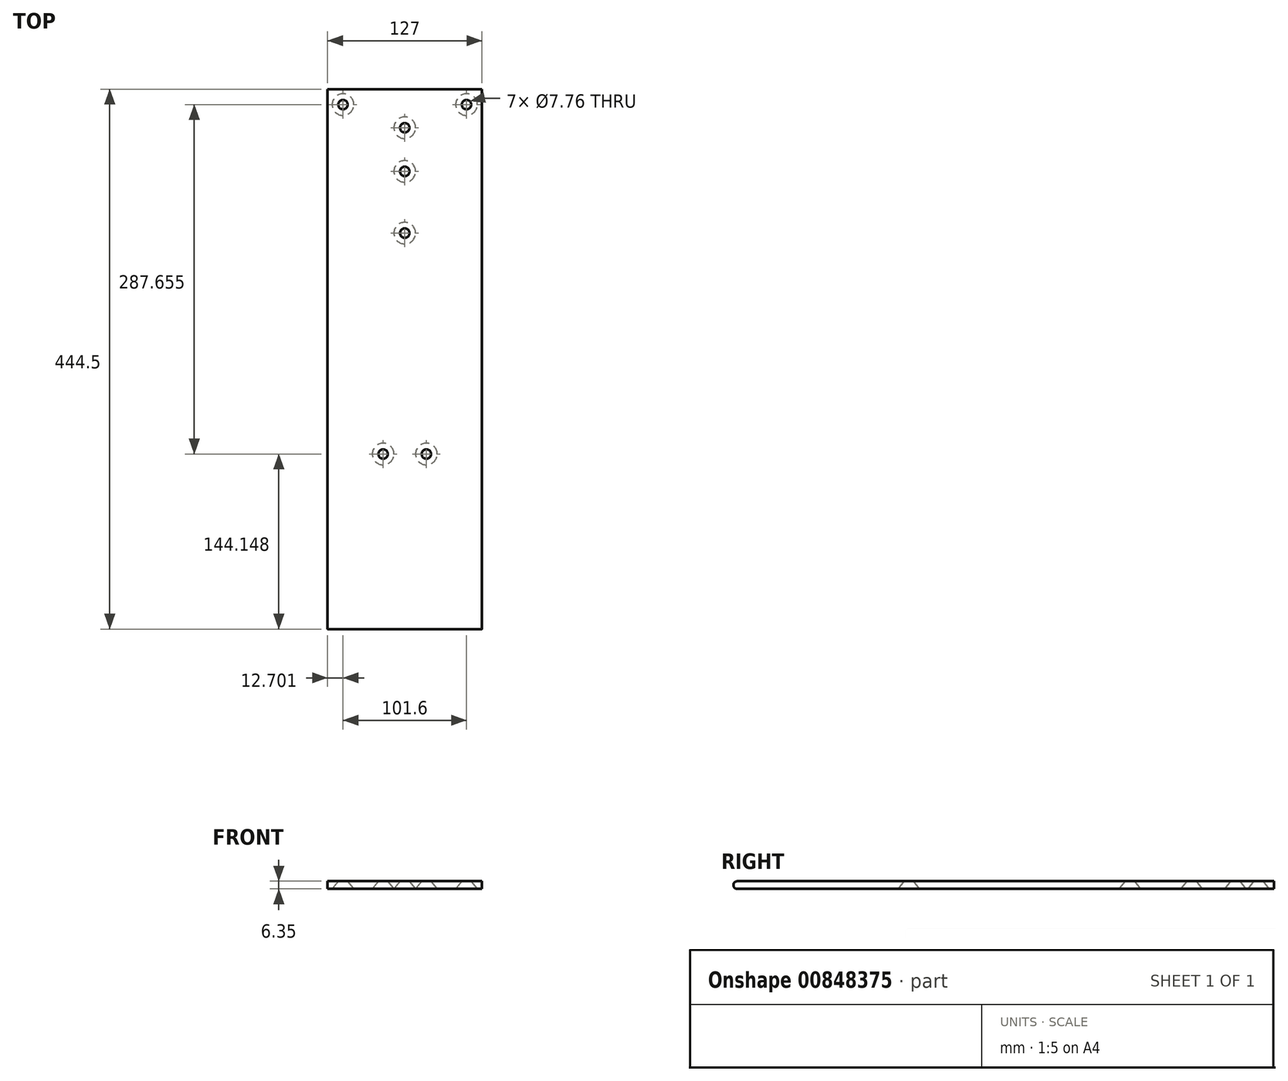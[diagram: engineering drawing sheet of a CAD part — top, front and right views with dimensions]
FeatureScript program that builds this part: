
annotation { "Feature Type Name" : "Feature", "Feature Type Description" : "" }
export const myFeature = defineFeature(function(context is Context, id is Id, definition is map)
    precondition{}
    {
        {
            var Q0;
            Q0=qCreatedBy(makeId("Top.planeOp"),FACE);
            var sketch = newSketch(context, id + "F0", { "sketchPlane" : qUnion([Q0])});
            skLineSegment(sketch, "E0.bottom", {"start": v(-72.87, 261.97) * mm, "end": v(54.13, 261.97) * mm});
            skLineSegment(sketch, "E0.top", {"start": v(-72.87, -182.53) * mm, "end": v(54.13, -182.53) * mm});
            skLineSegment(sketch, "E0.left", {"start": v(-72.87, 261.97) * mm, "end": v(-72.87, -182.53) * mm});
            skLineSegment(sketch, "E0.right", {"start": v(54.13, 261.97) * mm, "end": v(54.13, -182.53) * mm});
            skSolve(sketch);
        }
        {
            var Q0;
            Q0=makeQuery(id+"F0.imprint","IMPRINT",FACE,{"disambiguationData":[TD([[makeQuery(id+"F0.imprint","IMPRINT",EDGE,{"derivedFrom":sQuery(id+"F0.wireOp",EDGE,"E0.bottom")}),-1.0]])]});
            extrude(context, id + "F1", {"entities" : qUnion([Q0]), "depth" : 6.35 * mm, "offsetDistance" : 25.4 * mm});
        }
        {
            var Q0;
            Q0=makeQuery(id+"F1.opExtrude","CAP_FACE",FACE,{"disambiguationData":[OSD([sQuery(id+"F0.wireOp",EDGE,"E0.bottom"),sQuery(id+"F0.wireOp",EDGE,"E0.top"),sQuery(id+"F0.wireOp",EDGE,"E0.left"),sQuery(id+"F0.wireOp",EDGE,"E0.right")])],"isStart":false});
            var sketch = newSketch(context, id + "F2", { "sketchPlane" : qUnion([Q0])});
            skLineSegment(sketch, "E1", {"start": v(35.72, 199.74) * mm, "end": v(19.2, 185.77) * mm});
            skLineSegment(sketch, "E2", {"start": v(-54.45, 199.74) * mm, "end": v(-37.94, 185.77) * mm});
            skLineSegment(sketch, "E3", {"start": v(35.72, 148.94) * mm, "end": v(19.2, 134.97) * mm});
            skLineSegment(sketch, "E4", {"start": v(35.72, 91.8) * mm, "end": v(9.05, 69.23) * mm});
            skLineSegment(sketch, "E5", {"start": v(-54.45, 139.42) * mm, "end": v(-9.37, 101.27) * mm});
            skLineSegment(sketch, "E6", {"start": v(-54.45, 88.62) * mm, "end": v(-27.8, 66.06) * mm});
            skLineSegment(sketch, "E7", {"start": v(-28.42, -163.48) * mm, "end": v(-56.13, -138.08) * mm});
            skLineSegment(sketch, "E8", {"start": v(-9.37, -128.55) * mm, "end": v(-47.47, -93.63) * mm});
            skLineSegment(sketch, "E9", {"start": v(16.03, -106.33) * mm, "end": v(31.27, -87.91) * mm});
            skLineSegment(sketch, "E10", {"start": v(-9.37, -80.93) * mm, "end": v(1.43, -68.23) * mm});
            skLineSegment(sketch, "E11", {"start": v(9.68, -163.48) * mm, "end": v(35.08, -138.08) * mm});
            skArc(sketch, "E12.0.startCap", {"start": v(26.49, 210.65) * mm, "mid": v(46.62, 208.97) * mm, "end": v(44.95, 188.84) * mm});
            skArc(sketch, "E12.0.endCap", {"start": v(28.44, 174.87) * mm, "mid": v(8.3, 176.54) * mm, "end": v(9.98, 196.68) * mm});
            skLineSegment(sketch, "E12.0.left", {"start": v(44.95, 188.84) * mm, "end": v(28.44, 174.87) * mm});
            skLineSegment(sketch, "E12.0.right", {"start": v(26.49, 210.65) * mm, "end": v(9.98, 196.68) * mm});
            skArc(sketch, "E12.1.startCap", {"start": v(-63.68, 188.84) * mm, "mid": v(-65.36, 208.97) * mm, "end": v(-45.22, 210.65) * mm});
            skArc(sketch, "E12.1.endCap", {"start": v(-28.71, 196.68) * mm, "mid": v(-27.04, 176.54) * mm, "end": v(-47.17, 174.87) * mm});
            skLineSegment(sketch, "E12.1.left", {"start": v(-45.22, 210.65) * mm, "end": v(-28.71, 196.68) * mm});
            skLineSegment(sketch, "E12.1.right", {"start": v(-63.68, 188.84) * mm, "end": v(-47.17, 174.87) * mm});
            skArc(sketch, "E12.2.startCap", {"start": v(-63.68, 128.51) * mm, "mid": v(-65.36, 148.65) * mm, "end": v(-45.22, 150.32) * mm});
            skArc(sketch, "E12.2.endCap", {"start": v(-0.14, 112.18) * mm, "mid": v(1.54, 92.04) * mm, "end": v(-18.6, 90.36) * mm});
            skLineSegment(sketch, "E12.2.left", {"start": v(-45.22, 150.32) * mm, "end": v(-0.14, 112.18) * mm});
            skLineSegment(sketch, "E12.2.right", {"start": v(-63.68, 128.51) * mm, "end": v(-18.6, 90.36) * mm});
            skArc(sketch, "E12.3.startCap", {"start": v(26.49, 159.85) * mm, "mid": v(46.62, 158.17) * mm, "end": v(44.95, 138.04) * mm});
            skArc(sketch, "E12.3.endCap", {"start": v(28.44, 124.07) * mm, "mid": v(8.3, 125.74) * mm, "end": v(9.98, 145.88) * mm});
            skLineSegment(sketch, "E12.3.left", {"start": v(44.95, 138.04) * mm, "end": v(28.44, 124.07) * mm});
            skLineSegment(sketch, "E12.3.right", {"start": v(26.49, 159.85) * mm, "end": v(9.98, 145.88) * mm});
            skArc(sketch, "E12.4.startCap", {"start": v(-63.68, 77.71) * mm, "mid": v(-65.36, 97.85) * mm, "end": v(-45.22, 99.52) * mm});
            skArc(sketch, "E12.4.endCap", {"start": v(-18.56, 76.97) * mm, "mid": v(-16.89, 56.83) * mm, "end": v(-37.02, 55.15) * mm});
            skLineSegment(sketch, "E12.4.left", {"start": v(-45.22, 99.52) * mm, "end": v(-18.56, 76.97) * mm});
            skLineSegment(sketch, "E12.4.right", {"start": v(-63.68, 77.71) * mm, "end": v(-37.02, 55.15) * mm});
            skArc(sketch, "E12.5.startCap", {"start": v(26.49, 102.7) * mm, "mid": v(46.62, 101.02) * mm, "end": v(44.95, 80.89) * mm});
            skArc(sketch, "E12.5.endCap", {"start": v(18.28, 58.33) * mm, "mid": v(-1.85, 60) * mm, "end": v(-0.17, 80.14) * mm});
            skLineSegment(sketch, "E12.5.left", {"start": v(44.95, 80.89) * mm, "end": v(18.28, 58.33) * mm});
            skLineSegment(sketch, "E12.5.right", {"start": v(26.49, 102.7) * mm, "end": v(-0.17, 80.14) * mm});
            skArc(sketch, "E12.6.startCap", {"start": v(1.52, -90.18) * mm, "mid": v(-18.62, -91.81) * mm, "end": v(-20.26, -71.67) * mm});
            skArc(sketch, "E12.6.endCap", {"start": v(-9.46, -58.97) * mm, "mid": v(10.68, -57.34) * mm, "end": v(12.31, -77.48) * mm});
            skLineSegment(sketch, "E12.6.left", {"start": v(-20.26, -71.67) * mm, "end": v(-9.46, -58.97) * mm});
            skLineSegment(sketch, "E12.6.right", {"start": v(1.52, -90.18) * mm, "end": v(12.31, -77.48) * mm});
            skArc(sketch, "E12.7.startCap", {"start": v(27.04, -115.44) * mm, "mid": v(6.92, -117.33) * mm, "end": v(5.02, -97.22) * mm});
            skArc(sketch, "E12.7.endCap", {"start": v(20.26, -78.8) * mm, "mid": v(40.38, -76.9) * mm, "end": v(42.28, -97.02) * mm});
            skLineSegment(sketch, "E12.7.left", {"start": v(5.02, -97.22) * mm, "end": v(20.26, -78.8) * mm});
            skLineSegment(sketch, "E12.7.right", {"start": v(27.04, -115.44) * mm, "end": v(42.28, -97.02) * mm});
            skArc(sketch, "E12.8.startCap", {"start": v(0.29, -118.02) * mm, "mid": v(1.16, -138.2) * mm, "end": v(-19.02, -139.08) * mm});
            skArc(sketch, "E12.8.endCap", {"start": v(-57.12, -104.16) * mm, "mid": v(-58, -83.97) * mm, "end": v(-37.81, -83.1) * mm});
            skLineSegment(sketch, "E12.8.left", {"start": v(-19.02, -139.08) * mm, "end": v(-57.12, -104.16) * mm});
            skLineSegment(sketch, "E12.8.right", {"start": v(0.29, -118.02) * mm, "end": v(-37.81, -83.1) * mm});
            skArc(sketch, "E12.9.startCap", {"start": v(-18.76, -152.94) * mm, "mid": v(-17.89, -173.13) * mm, "end": v(-38.07, -174) * mm});
            skArc(sketch, "E12.9.endCap", {"start": v(-65.78, -148.6) * mm, "mid": v(-66.66, -128.42) * mm, "end": v(-46.47, -127.54) * mm});
            skLineSegment(sketch, "E12.9.left", {"start": v(-38.07, -174) * mm, "end": v(-65.78, -148.6) * mm});
            skLineSegment(sketch, "E12.9.right", {"start": v(-18.76, -152.94) * mm, "end": v(-46.47, -127.54) * mm});
            skArc(sketch, "E12.10.startCap", {"start": v(19.78, -173.58) * mm, "mid": v(-0.42, -173.58) * mm, "end": v(-0.42, -153.37) * mm});
            skArc(sketch, "E12.10.endCap", {"start": v(24.98, -127.97) * mm, "mid": v(45.18, -127.97) * mm, "end": v(45.18, -148.18) * mm});
            skLineSegment(sketch, "E12.10.left", {"start": v(-0.42, -153.37) * mm, "end": v(24.98, -127.97) * mm});
            skLineSegment(sketch, "E12.10.right", {"start": v(19.78, -173.58) * mm, "end": v(45.18, -148.18) * mm});
            skSolve(sketch);
        }
        {
            var Q0;
            Q0=makeQuery(id+"F1.opExtrude","CAP_FACE",FACE,{"disambiguationData":[OSD([sQuery(id+"F0.wireOp",EDGE,"E0.bottom"),sQuery(id+"F0.wireOp",EDGE,"E0.top"),sQuery(id+"F0.wireOp",EDGE,"E0.left"),sQuery(id+"F0.wireOp",EDGE,"E0.right")])],"isStart":true});
            var sketch = newSketch(context, id + "F3", { "sketchPlane" : qUnion([Q0])});
            skPoint(sketch, "E13", {"position": v(41.43, -249.27) * mm});
            skPoint(sketch, "E14", {"position": v(-60.17, -249.27) * mm});
            skPoint(sketch, "E15", {"position": v(-9.37, -230.22) * mm});
            skPoint(sketch, "E15.positionSnap0", {"position": v(-9.37, -261.97) * mm});
            skPoint(sketch, "E16", {"position": v(-9.37, -194.28) * mm});
            skPoint(sketch, "E17", {"position": v(-9.37, -143.48) * mm});
            skPoint(sketch, "E18", {"position": v(8.41, 38.38) * mm});
            skPoint(sketch, "E19", {"position": v(-27.15, 38.38) * mm});
            skSolve(sketch);
        }
        {
            var Q0;
            Q0=sQuery(id+"F3.wireOp",VERTEX,"E13");
            var Q1;
            Q1=sQuery(id+"F3.wireOp",VERTEX,"E15");
            var Q2;
            Q2=sQuery(id+"F3.wireOp",VERTEX,"E14");
            var Q3;
            Q3=sQuery(id+"F3.wireOp",VERTEX,"E16");
            var Q4;
            Q4=sQuery(id+"F3.wireOp",VERTEX,"E17");
            var Q5;
            Q5=sQuery(id+"F3.wireOp",VERTEX,"E18");
            var Q6;
            Q6=sQuery(id+"F3.wireOp",VERTEX,"E19");
            var Q7;
            Q7=makeQuery(id+"F1.opExtrude","SWEPT_BODY",BODY,{"disambiguationData":[OSD([sQuery(id+"F0.wireOp",EDGE,"E0.bottom"),sQuery(id+"F0.wireOp",EDGE,"E0.top"),sQuery(id+"F0.wireOp",EDGE,"E0.left"),sQuery(id+"F0.wireOp",EDGE,"E0.right")])]});
            hole(context, id + "F4", {"style" : HoleStyle.C_SINK, "endStyle" : HoleEndStyle.BLIND, "holeDiameter" : 7.76 * mm, "cSinkDiameter" : 17.78 * mm, "cSinkAngle" : 77 * degree, "majorDiameter" : 6.35 * mm, "holeDepth" : 9.52 * mm, "isTappedThrough" : true, "tappedDepth" : 12.7 * mm, "tapClearance" : 3, "locations" : qUnion([Q0, Q1, Q2, Q3, Q4, Q5, Q6]), "scope" : qUnion([Q7])});
        }
        {
            var Q0;
            Q0=makeQuery(id+"F1.opExtrude","CAP_EDGE",EDGE,{"disambiguationData":[OSD([sQuery(id+"F0.wireOp",EDGE,"E0.top")])],"isStart":false});
            var Q1;
            Q1=makeQuery(id+"F1.opExtrude","CAP_EDGE",EDGE,{"disambiguationData":[OSD([sQuery(id+"F0.wireOp",EDGE,"E0.top")])],"isStart":true});
            fillet(context, id + "F5", {"entities" : qUnion([Q0, Q1]), "radius" : 3.17 * mm, "tangentPropagation" : true, "allowEdgeOverflow" : false});
        }
    });
